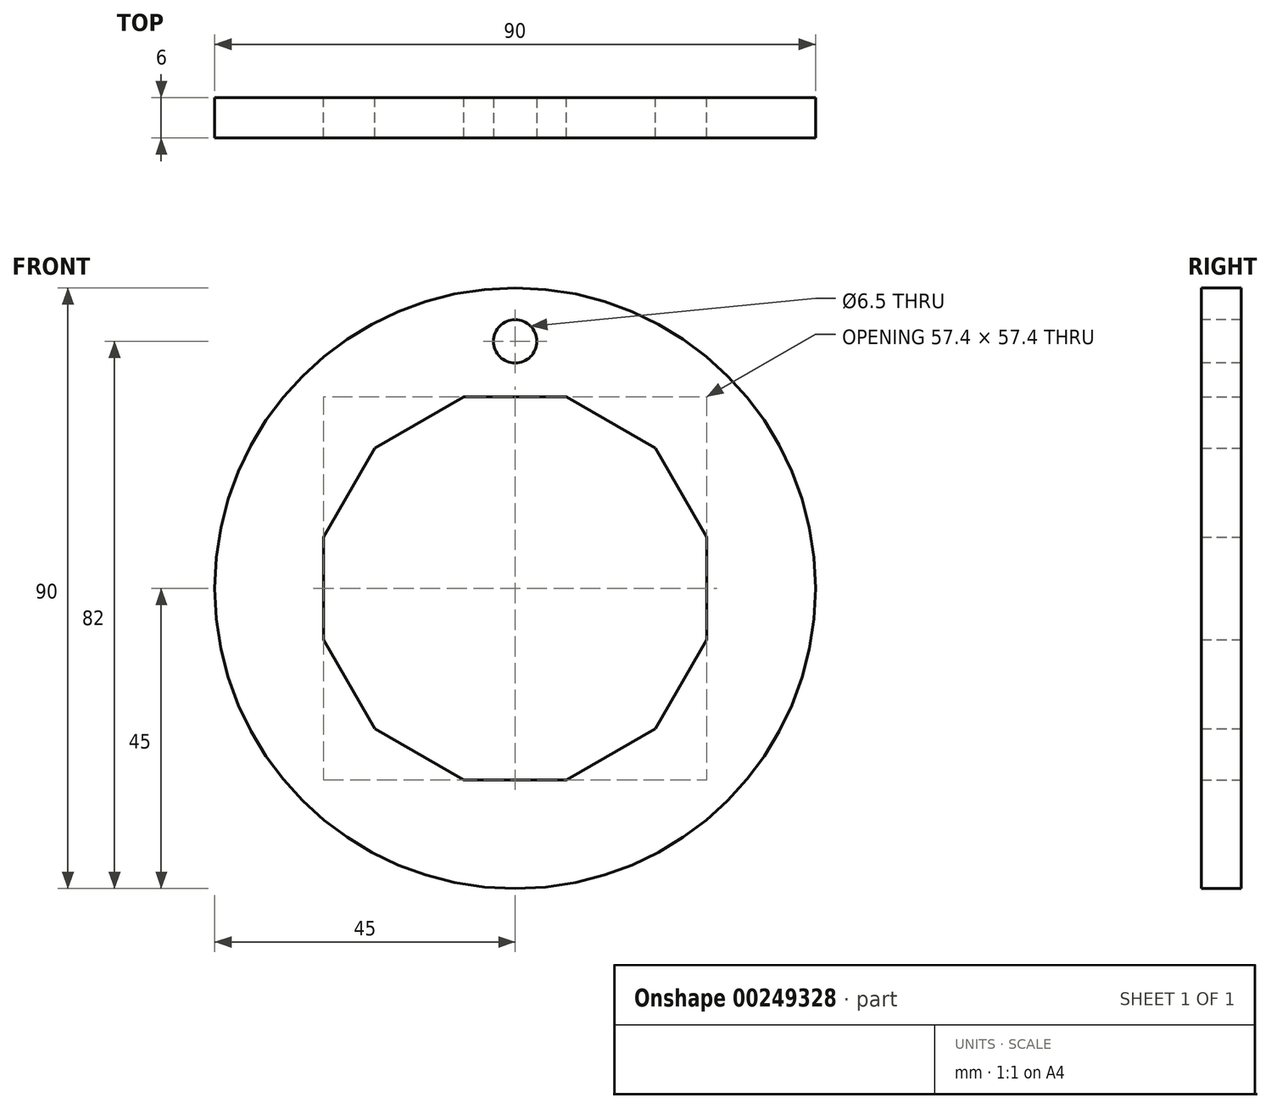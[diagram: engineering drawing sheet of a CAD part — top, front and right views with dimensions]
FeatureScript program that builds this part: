
annotation { "Feature Type Name" : "Feature", "Feature Type Description" : "" }
export const myFeature = defineFeature(function(context is Context, id is Id, definition is map)
    precondition{}
    {
        {
            var Q0;
            Q0=qCreatedBy(makeId("Front.planeOp"),FACE);
            var sketch = newSketch(context, id + "F0", { "sketchPlane" : qUnion([Q0])});
            skCircle(sketch, "E0.cCircle", {"center": v(0, 0) * mm, "radius": 28.7 * mm, "construction": true});
            skLineSegment(sketch, "E0.0", {"start": v(-7.7, 28.7) * mm, "end": v(7.7, 28.7) * mm});
            skLineSegment(sketch, "E0.1", {"start": v(7.7, 28.7) * mm, "end": v(21, 21) * mm});
            skLineSegment(sketch, "E0.2", {"start": v(21, 21) * mm, "end": v(28.7, 7.7) * mm});
            skLineSegment(sketch, "E0.3", {"start": v(28.7, 7.7) * mm, "end": v(28.7, -7.7) * mm});
            skLineSegment(sketch, "E0.4", {"start": v(28.7, -7.7) * mm, "end": v(21, -21) * mm});
            skLineSegment(sketch, "E0.5", {"start": v(21, -21) * mm, "end": v(7.7, -28.7) * mm});
            skLineSegment(sketch, "E0.6", {"start": v(7.7, -28.7) * mm, "end": v(-7.7, -28.7) * mm});
            skLineSegment(sketch, "E0.7", {"start": v(-7.7, -28.7) * mm, "end": v(-21, -21) * mm});
            skLineSegment(sketch, "E0.8", {"start": v(-21, -21) * mm, "end": v(-28.7, -7.7) * mm});
            skLineSegment(sketch, "E0.9", {"start": v(-28.7, -7.7) * mm, "end": v(-28.7, 7.7) * mm});
            skLineSegment(sketch, "E0.10", {"start": v(-28.7, 7.7) * mm, "end": v(-21, 21) * mm});
            skLineSegment(sketch, "E0.11", {"start": v(-21, 21) * mm, "end": v(-7.7, 28.7) * mm});
            skPoint(sketch, "E0.0.midPoint", {"position": v(0, 28.7) * mm});
            skCircle(sketch, "E1", {"center": v(0, 0) * mm, "radius": 45 * mm});
            skSolve(sketch);
        }
        {
            var Q0;
            Q0=makeQuery(id+"F0.imprint","IMPRINT",FACE,{"disambiguationData":[TD([[makeQuery(id+"F0.imprint","IMPRINT",EDGE,{"derivedFrom":sQuery(id+"F0.wireOp",EDGE,"E0.0")}),1.0]])]});
            extrude(context, id + "F1", {"entities" : qUnion([Q0]), "depth" : 6 * mm});
        }
        {
            var Q0;
            Q0=makeQuery(id+"F1.opExtrude","CAP_FACE",FACE,{"disambiguationData":[OSD([sQuery(id+"F0.wireOp",EDGE,"E0.0"),sQuery(id+"F0.wireOp",EDGE,"E0.1"),sQuery(id+"F0.wireOp",EDGE,"E0.2"),sQuery(id+"F0.wireOp",EDGE,"E0.3"),sQuery(id+"F0.wireOp",EDGE,"E0.4"),sQuery(id+"F0.wireOp",EDGE,"E0.5"),sQuery(id+"F0.wireOp",EDGE,"E0.6"),sQuery(id+"F0.wireOp",EDGE,"E0.7"),sQuery(id+"F0.wireOp",EDGE,"E0.8"),sQuery(id+"F0.wireOp",EDGE,"E0.9"),sQuery(id+"F0.wireOp",EDGE,"E0.10"),sQuery(id+"F0.wireOp",EDGE,"E0.11"),sQuery(id+"F0.wireOp",EDGE,"E1")])],"isStart":false});
            var sketch = newSketch(context, id + "F2", { "sketchPlane" : qUnion([Q0])});
            skCircle(sketch, "E2", {"center": v(0, 37) * mm, "radius": 3.25 * mm});
            skSolve(sketch);
        }
        {
            var Q0;
            Q0=makeQuery(id+"F2.imprint","IMPRINT",FACE,{"disambiguationData":[TD([[makeQuery(id+"F2.imprint","IMPRINT",EDGE,{"derivedFrom":sQuery(id+"F2.wireOp",EDGE,"E2")}),1.0]])]});
            extrude(context, id + "F3", {"entities" : qUnion([Q0]), "operationType" : NewBodyOperationType.REMOVE, "oppositeDirection" : true, "depth" : 25 * mm, "symmetric" : true});
        }
    });
